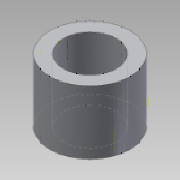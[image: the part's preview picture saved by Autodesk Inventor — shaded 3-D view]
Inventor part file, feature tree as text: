
AUTODESK INVENTOR PART (.ipt)
format: ipt  version: 2013 SP2 (Build 170200200, 200)  size: 96,256 bytes
history: native  units: mm
features: extrude x1, sketch x1
ambient origin geometry x8: Origin, YZ Plane, XZ Plane, XY Plane, X Axis, Y Axis, Z Axis, Center Point
bodies: Solid1 (feature_tree)
feature tree (2):
  extrude  "Extrusion1"  Depth=8.0mm
  sketch  "Sketch1"  dims[d0=5.3mm d1=8.0mm d3=0.0mm]
